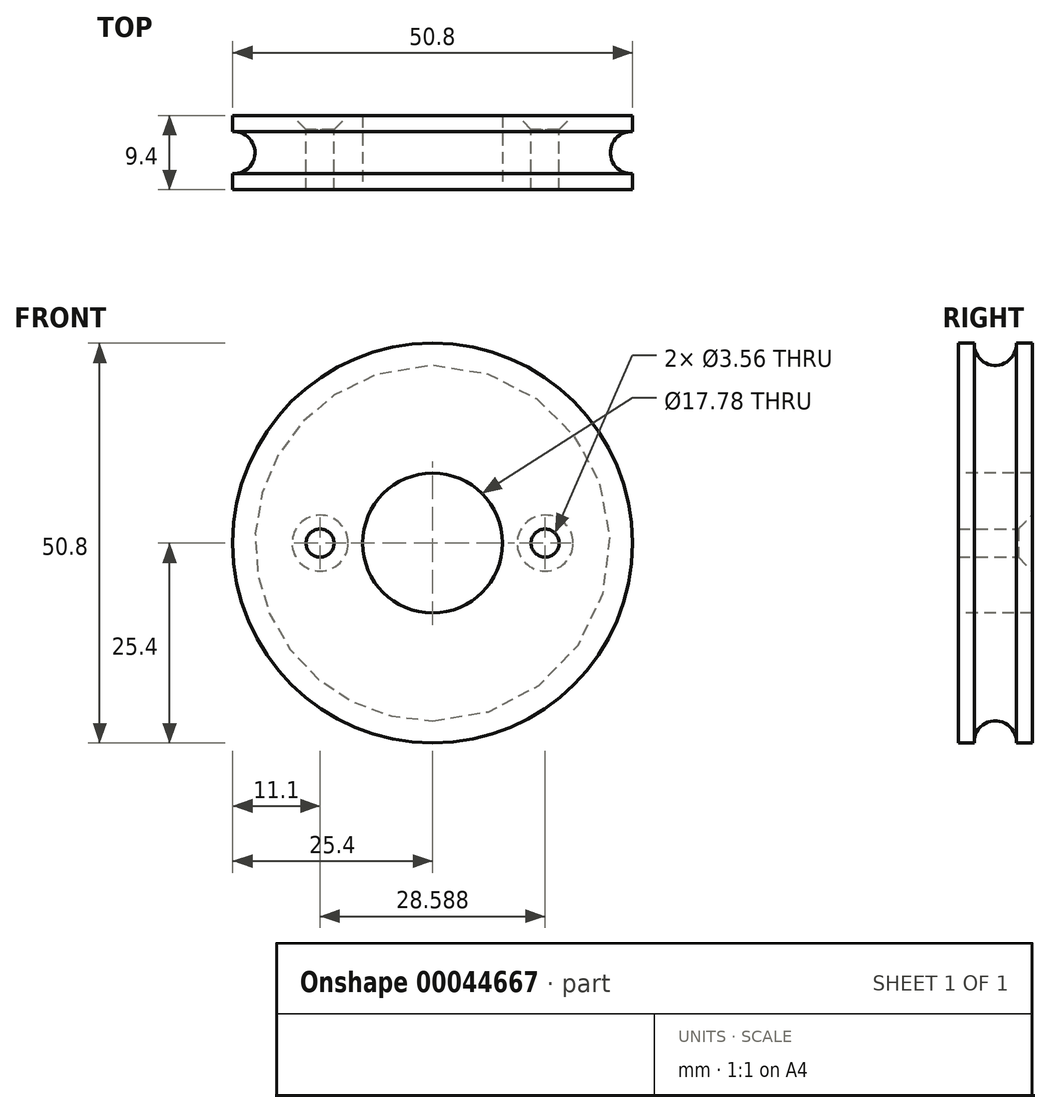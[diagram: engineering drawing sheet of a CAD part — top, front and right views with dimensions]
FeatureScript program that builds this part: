
annotation { "Feature Type Name" : "Feature", "Feature Type Description" : "" }
export const myFeature = defineFeature(function(context is Context, id is Id, definition is map)
    precondition{}
    {
        {
            var Q0;
            Q0=qCreatedBy(makeId("Right.planeOp"),FACE);
            var sketch = newSketch(context, id + "F0", { "sketchPlane" : qUnion([Q0])});
            skLineSegment(sketch, "E0", {"start": v(-7.37, 25.4) * mm, "end": v(-9.4, 25.4) * mm});
            skLineSegment(sketch, "E1", {"start": v(-9.4, 25.4) * mm, "end": v(-9.4, 0) * mm});
            skLineSegment(sketch, "E2", {"start": v(-9.4, 0) * mm, "end": v(0, 0) * mm});
            skLineSegment(sketch, "E3", {"start": v(0, 0) * mm, "end": v(0, 25.4) * mm});
            skLineSegment(sketch, "E4", {"start": v(0, 25.4) * mm, "end": v(-2.03, 25.4) * mm});
            skArc(sketch, "E5", {"start": v(-7.37, 25.4) * mm, "mid": v(-4.7, 22.57) * mm, "end": v(-2.03, 25.4) * mm});
            skSolve(sketch);
        }
        {
            var Q0;
            Q0=makeQuery(id+"F0.imprint","IMPRINT",FACE,{"disambiguationData":[TD([[makeQuery(id+"F0.imprint","IMPRINT",EDGE,{"derivedFrom":sQuery(id+"F0.wireOp",EDGE,"E0")}),1.0]])]});
            var Q1;
            Q1=sQuery(id+"F0.wireOp",EDGE,"E2");
            revolve(context, id + "F1", {"entities" : qUnion([Q0]), "axis" : qUnion([Q1]), "revolveType" : RevolveType.FULL});
        }
        {
            var Q0;
            Q0=qCreatedBy(makeId("Front.planeOp"),FACE);
            var sketch = newSketch(context, id + "F2", { "sketchPlane" : qUnion([Q0])});
            skPoint(sketch, "E6", {"position": v(14.29, 0) * mm});
            skPoint(sketch, "E7", {"position": v(-14.3, 0) * mm});
            skSolve(sketch);
        }
        {
            var Q0;
            Q0=sQuery(id+"F2.wireOp",VERTEX,"E6");
            var Q1;
            Q1=sQuery(id+"F2.wireOp",VERTEX,"E7");
            var Q2;
            Q2=makeQuery(id+"F1.opRevolve","SWEPT_BODY",BODY,{"disambiguationData":[OSD([sQuery(id+"F0.wireOp",EDGE,"E0"),sQuery(id+"F0.wireOp",EDGE,"E1"),sQuery(id+"F0.wireOp",EDGE,"E2"),sQuery(id+"F0.wireOp",EDGE,"E3"),sQuery(id+"F0.wireOp",EDGE,"E4"),sQuery(id+"F0.wireOp",EDGE,"E5")])]});
            hole(context, id + "F3", {"style" : HoleStyle.C_SINK, "holeDiameter" : 3.56 * mm, "cSinkDiameter" : 7.11 * mm, "endStyle" : HoleEndStyle.THROUGH, "oppositeDirection" : true, "locations" : qUnion([Q0, Q1]), "scope" : qUnion([Q2]), "cSinkAngle" : 90 * degree});
        }
        {
            var Q0;
            Q0=makeQuery(id+"F1.opRevolve","SWEPT_FACE",FACE,{"disambiguationData":[OSD([sQuery(id+"F0.wireOp",EDGE,"E1")])]});
            var sketch = newSketch(context, id + "F4", { "sketchPlane" : qUnion([Q0])});
            skPoint(sketch, "E8", {"position": v(0, 0) * mm});
            skSolve(sketch);
        }
        {
            var Q0;
            Q0=sQuery(id+"F4.wireOp",VERTEX,"E8");
            var Q1;
            Q1=makeQuery(id+"F1.opRevolve","SWEPT_BODY",BODY,{"disambiguationData":[OSD([sQuery(id+"F0.wireOp",EDGE,"E0"),sQuery(id+"F0.wireOp",EDGE,"E1"),sQuery(id+"F0.wireOp",EDGE,"E2"),sQuery(id+"F0.wireOp",EDGE,"E3"),sQuery(id+"F0.wireOp",EDGE,"E4"),sQuery(id+"F0.wireOp",EDGE,"E5")])]});
            hole(context, id + "F5", {"style" : HoleStyle.SIMPLE, "holeDiameter" : 17.78 * mm, "endStyle" : HoleEndStyle.THROUGH, "locations" : qUnion([Q0]), "scope" : qUnion([Q1])});
        }
    });
